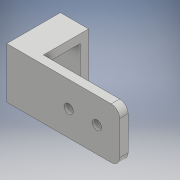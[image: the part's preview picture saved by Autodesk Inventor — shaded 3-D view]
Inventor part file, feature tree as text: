
AUTODESK INVENTOR PART (.ipt)
format: ipt  version: 2018 (Build 220112000, 112)  size: 131,072 bytes
history: native  units: mm
features: extrude x3, sketch x3, fillet x1
ambient origin geometry x8: Origin, YZ Plane, XZ Plane, XY Plane, X Axis, Y Axis, Z Axis, Center Point
bodies: Solid1 (feature_tree)
feature tree (7):
  extrude  "Extrusion1"  Depth=12.0mm
  extrude  "Extrusion2"  Depth=3.0mm
  extrude  "Extrusion3"  Depth=3.0mm
  fillet  "Fillet1"  Radius=10.0mm
  sketch  "Sketch1"  dims[d0=10.0mm d1=12.0mm]
  sketch  "Sketch2"  dims[d2=3.0mm d3=3.0mm]
  sketch  "Sketch3"  dims[d4=6.0mm d5=3.0mm d6=10.0mm d7=0.0mm d8=3.0mm d9=30.0mm d10=0.0mm d11=3.2mm d12=3.2mm d13=9.0mm d14=9.0mm d15=8.0mm d16=10.0mm d17=30.0mm d18=0.0mm d19=3.0mm]
